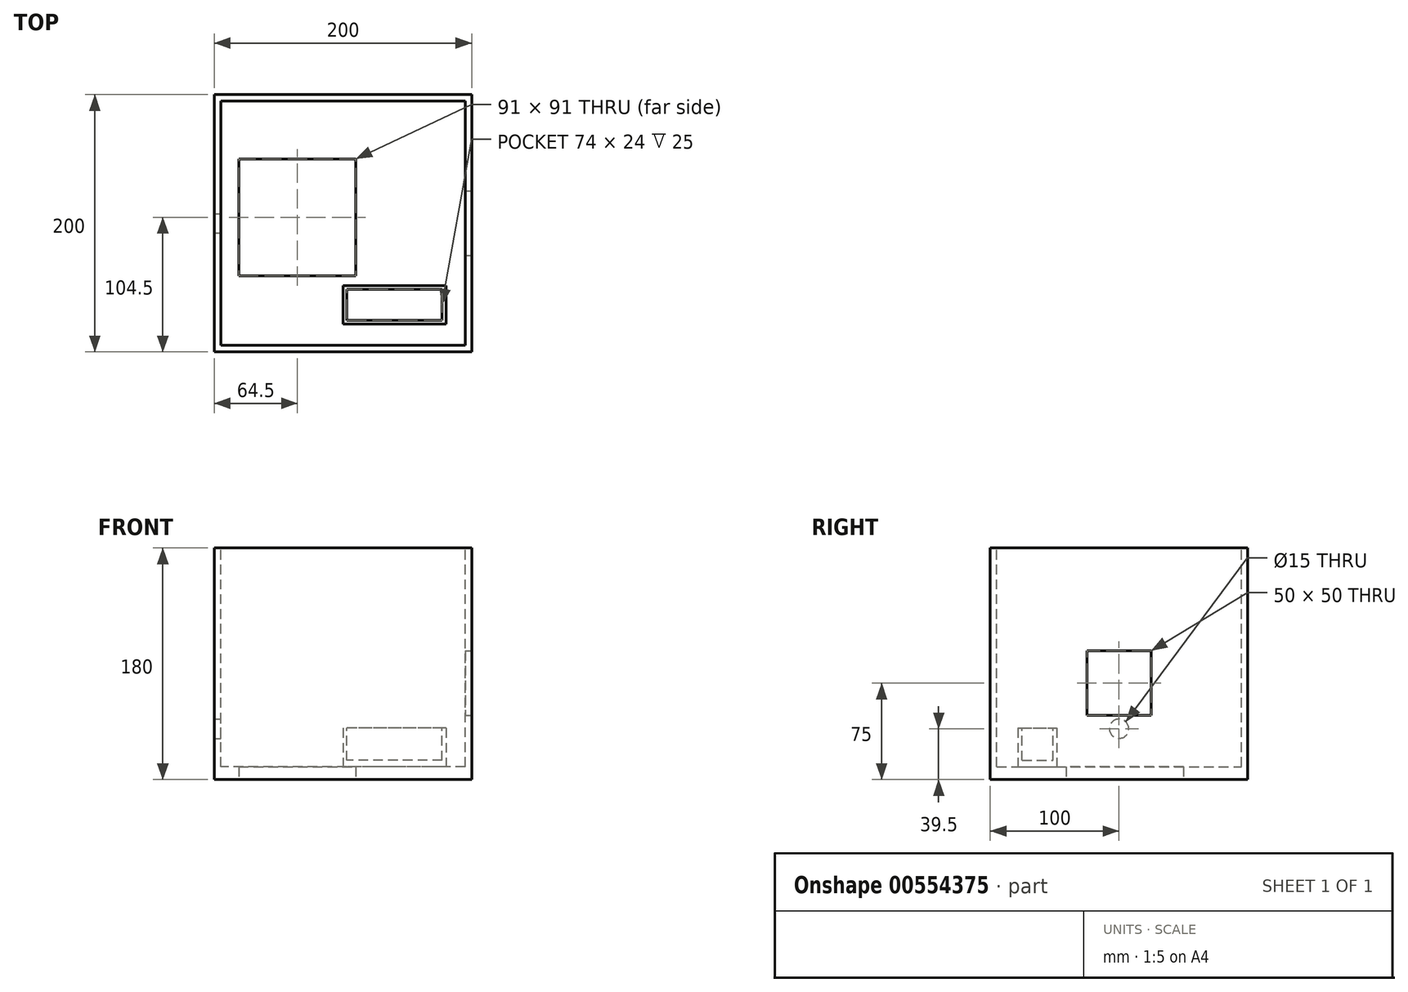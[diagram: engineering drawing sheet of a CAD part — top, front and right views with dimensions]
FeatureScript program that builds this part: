
annotation { "Feature Type Name" : "Feature", "Feature Type Description" : "" }
export const myFeature = defineFeature(function(context is Context, id is Id, definition is map)
    precondition{}
    {
        {
            var Q0;
            Q0=qCreatedBy(makeId("Top.planeOp"),FACE);
            var sketch = newSketch(context, id + "F0", { "sketchPlane" : qUnion([Q0])});
            skLineSegment(sketch, "E0.bottom", {"start": v(100, -100) * mm, "end": v(-100, -100) * mm});
            skLineSegment(sketch, "E0.top", {"start": v(100, 100) * mm, "end": v(-100, 100) * mm});
            skLineSegment(sketch, "E0.left", {"start": v(100, -100) * mm, "end": v(100, 100) * mm});
            skLineSegment(sketch, "E0.right", {"start": v(-100, -100) * mm, "end": v(-100, 100) * mm});
            skPoint(sketch, "E0.middle", {"position": v(0, 0) * mm});
            skSolve(sketch);
        }
        {
            var Q0;
            Q0=makeQuery(id+"F0.imprint","IMPRINT",FACE,{"disambiguationData":[TD([[makeQuery(id+"F0.imprint","IMPRINT",EDGE,{"derivedFrom":sQuery(id+"F0.wireOp",EDGE,"E0.bottom")}),-1.0]])]});
            extrude(context, id + "F1", {"entities" : qUnion([Q0]), "depth" : 180 * mm, "offsetDistance" : 25 * mm});
        }
        {
            var Q0;
            Q0=makeQuery(id+"F1.opExtrude","CAP_FACE",FACE,{"disambiguationData":[OSD([sQuery(id+"F0.wireOp",EDGE,"E0.bottom"),sQuery(id+"F0.wireOp",EDGE,"E0.top"),sQuery(id+"F0.wireOp",EDGE,"E0.left"),sQuery(id+"F0.wireOp",EDGE,"E0.right")])],"isStart":false});
            var sketch = newSketch(context, id + "F2", { "sketchPlane" : qUnion([Q0])});
            skLineSegment(sketch, "E1.0", {"start": v(95, 95) * mm, "end": v(-95, 95) * mm});
            skLineSegment(sketch, "E1.1", {"start": v(95, -95) * mm, "end": v(95, 95) * mm});
            skLineSegment(sketch, "E1.2", {"start": v(95, -95) * mm, "end": v(-95, -95) * mm});
            skLineSegment(sketch, "E1.3", {"start": v(-95, -95) * mm, "end": v(-95, 95) * mm});
            skSolve(sketch);
        }
        {
            var Q0;
            Q0=makeQuery(id+"F2.imprint","IMPRINT",FACE,{"disambiguationData":[TD([[makeQuery(id+"F2.imprint","IMPRINT",EDGE,{"derivedFrom":sQuery(id+"F2.wireOp",EDGE,"E1.0")}),1.0]])]});
            extrude(context, id + "F3", {"entities" : qUnion([Q0]), "operationType" : NewBodyOperationType.REMOVE, "oppositeDirection" : true, "depth" : 170 * mm, "offsetDistance" : 25 * mm});
        }
        {
            var Q0;
            Q0=makeQuery(id+"F1.opExtrude","SWEPT_FACE",FACE,{"disambiguationData":[OSD([sQuery(id+"F0.wireOp",EDGE,"E0.left")])]});
            var sketch = newSketch(context, id + "F4", { "sketchPlane" : qUnion([Q0])});
            skLineSegment(sketch, "E2.bottom", {"start": v(25, 100) * mm, "end": v(-25, 100) * mm});
            skLineSegment(sketch, "E2.top", {"start": v(25, 50) * mm, "end": v(-25, 50) * mm});
            skLineSegment(sketch, "E2.left", {"start": v(25, 100) * mm, "end": v(25, 50) * mm});
            skLineSegment(sketch, "E2.right", {"start": v(-25, 100) * mm, "end": v(-25, 50) * mm});
            skSolve(sketch);
        }
        {
            var Q0;
            Q0=makeQuery(id+"F4.imprint","IMPRINT",FACE,{"disambiguationData":[TD([[makeQuery(id+"F4.imprint","IMPRINT",EDGE,{"derivedFrom":sQuery(id+"F4.wireOp",EDGE,"E2.bottom")}),1.0]])]});
            extrude(context, id + "F5", {"entities" : qUnion([Q0]), "operationType" : NewBodyOperationType.REMOVE, "oppositeDirection" : true, "depth" : 8 * mm, "offsetDistance" : 25 * mm});
        }
        {
            var Q0;
            Q0=makeQuery(id+"F3.boolean.opBoolean","COPY",FACE,{"derivedFrom":makeQuery(id+"F3.opExtrude","CAP_FACE",FACE,{"disambiguationData":[OSD([sQuery(id+"F2.wireOp",EDGE,"E1.0"),sQuery(id+"F2.wireOp",EDGE,"E1.1"),sQuery(id+"F2.wireOp",EDGE,"E1.2"),sQuery(id+"F2.wireOp",EDGE,"E1.3")])],"isStart":false})});
            var sketch = newSketch(context, id + "F6", { "sketchPlane" : qUnion([Q0])});
            skLineSegment(sketch, "E3.bottom", {"start": v(80, -78.4) * mm, "end": v(0, -78.4) * mm});
            skLineSegment(sketch, "E3.top", {"start": v(80, -48.4) * mm, "end": v(0, -48.4) * mm});
            skLineSegment(sketch, "E3.left", {"start": v(80, -78.4) * mm, "end": v(80, -48.4) * mm});
            skLineSegment(sketch, "E3.right", {"start": v(0, -78.4) * mm, "end": v(0, -48.4) * mm});
            skSolve(sketch);
        }
        {
            var Q0;
            Q0=makeQuery(id+"F6.imprint","IMPRINT",FACE,{"disambiguationData":[TD([[makeQuery(id+"F6.imprint","IMPRINT",EDGE,{"derivedFrom":sQuery(id+"F6.wireOp",EDGE,"E3.bottom")}),-1.0]])]});
            extrude(context, id + "F7", {"entities" : qUnion([Q0]), "operationType" : NewBodyOperationType.ADD, "depth" : 30 * mm, "offsetDistance" : 25 * mm});
        }
        {
            var Q0;
            Q0=makeQuery(id+"F7.opExtrude","CAP_FACE",FACE,{"disambiguationData":[OSD([sQuery(id+"F6.wireOp",EDGE,"E3.bottom"),sQuery(id+"F6.wireOp",EDGE,"E3.top"),sQuery(id+"F6.wireOp",EDGE,"E3.left"),sQuery(id+"F6.wireOp",EDGE,"E3.right")])],"isStart":false});
            var sketch = newSketch(context, id + "F8", { "sketchPlane" : qUnion([Q0])});
            skLineSegment(sketch, "E4.0", {"start": v(77, -51.4) * mm, "end": v(3, -51.4) * mm});
            skLineSegment(sketch, "E4.1", {"start": v(77, -75.4) * mm, "end": v(77, -51.4) * mm});
            skLineSegment(sketch, "E4.2", {"start": v(77, -75.4) * mm, "end": v(3, -75.4) * mm});
            skLineSegment(sketch, "E4.3", {"start": v(3, -75.4) * mm, "end": v(3, -51.4) * mm});
            skSolve(sketch);
        }
        {
            var Q0;
            Q0=makeQuery(id+"F8.imprint","IMPRINT",FACE,{"disambiguationData":[TD([[makeQuery(id+"F8.imprint","IMPRINT",EDGE,{"derivedFrom":sQuery(id+"F8.wireOp",EDGE,"E4.0")}),1.0]])]});
            extrude(context, id + "F9", {"entities" : qUnion([Q0]), "operationType" : NewBodyOperationType.REMOVE, "oppositeDirection" : true, "depth" : 25 * mm, "offsetDistance" : 25 * mm});
        }
        {
            var Q0;
            Q0=qCreatedBy(makeId("Top.planeOp"),FACE);
            var sketch = newSketch(context, id + "F10", { "sketchPlane" : qUnion([Q0])});
            skLineSegment(sketch, "E5.bottom", {"start": v(10, -41) * mm, "end": v(-81, -41) * mm});
            skLineSegment(sketch, "E5.top", {"start": v(10, 50) * mm, "end": v(-81, 50) * mm});
            skLineSegment(sketch, "E5.left", {"start": v(10, -41) * mm, "end": v(10, 50) * mm});
            skLineSegment(sketch, "E5.right", {"start": v(-81, -41) * mm, "end": v(-81, 50) * mm});
            skSolve(sketch);
        }
        {
            var Q0;
            Q0 = qSketchRegion(id + "F10", true);
            extrude(context, id + "F11", {"entities" : qUnion([Q0]), "operationType" : NewBodyOperationType.REMOVE, "depth" : 25 * mm, "offsetDistance" : 25 * mm});
        }
        {
            var Q0;
            Q0=makeQuery(id+"F3.boolean.opBoolean","COPY",FACE,{"derivedFrom":makeQuery(id+"F3.opExtrude","SWEPT_FACE",FACE,{"disambiguationData":[OSD([sQuery(id+"F2.wireOp",EDGE,"E1.3")])]})});
            var sketch = newSketch(context, id + "F12", { "sketchPlane" : qUnion([Q0])});
            skCircle(sketch, "E6", {"center": v(0, 39.5) * mm, "radius": 7.5 * mm});
            skSolve(sketch);
        }
        {
            var Q0;
            Q0 = qSketchRegion(id + "F12", true);
            extrude(context, id + "F13", {"entities" : qUnion([Q0]), "operationType" : NewBodyOperationType.REMOVE, "oppositeDirection" : true, "depth" : 25 * mm, "offsetDistance" : 25 * mm});
        }
    });
